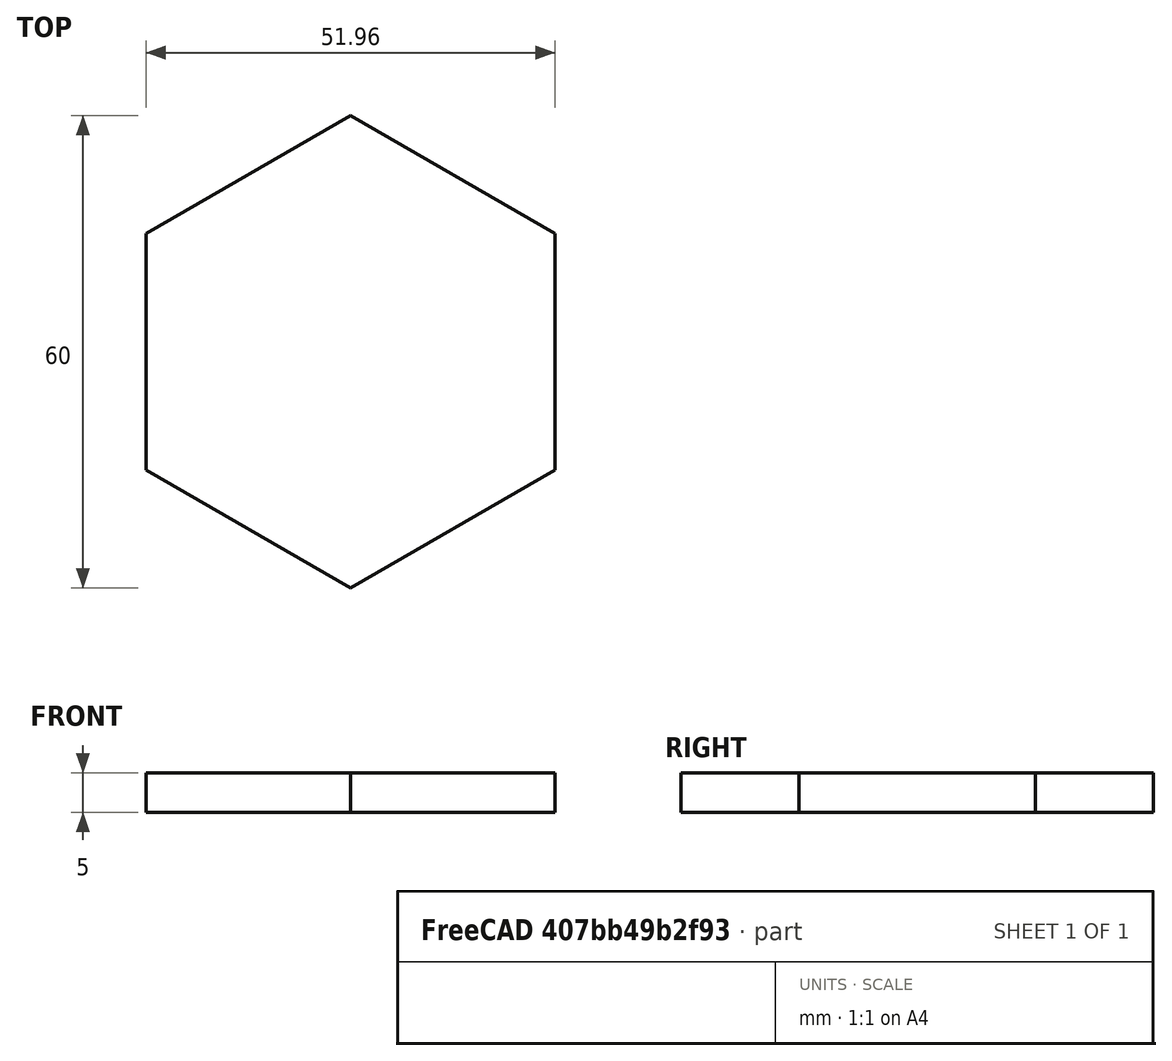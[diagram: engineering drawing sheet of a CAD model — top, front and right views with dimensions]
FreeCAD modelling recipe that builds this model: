
FCSTD DOCUMENT  (FreeCAD 0.19R)
Label: BodyTest
License: Creative Commons Attribution-ShareAlike
LicenseURL: http://creativecommons.org/licenses/by-sa/4.0/
objects: Sketcher::SketchObject×1, PartDesign::Pad×1, PartDesign::Body×1
note: 4 computed .brp shape members not serialized (recipe doc carries the construction recipe); baked Part::Feature solids carry a one-line shape summary decoded from their .brp

FEATURE [Sketcher::SketchObject] Sketch
  MapMode = 5
  Support = -> [XY_Plane001]
  sketch-geometry (7):
    g0: LineSegment StartX=25.9808 StartY=15 StartZ=0 EndX=3.6e-15 EndY=30 EndZ=0
    g1: LineSegment StartX=2e-15 StartY=30 StartZ=0 EndX=-25.9808 EndY=15 EndZ=0
    g2: LineSegment StartX=-25.9808 StartY=15 StartZ=0 EndX=-25.9808 EndY=-15 EndZ=0
    g3: LineSegment StartX=-25.9808 StartY=-15 StartZ=0 EndX=0 EndY=-30 EndZ=0
    g4: LineSegment StartX=0 StartY=-30 StartZ=0 EndX=25.9808 EndY=-15 EndZ=0
    g5: LineSegment StartX=25.9808 StartY=-15 StartZ=0 EndX=25.9808 EndY=15 EndZ=0
    g6: Circle [constr] CenterX=0 CenterY=0 CenterZ=0 NormalX=0 NormalY=0 NormalZ=1 AngleXU=0 Radius=30
  constraints (16):
    c: Coincident(g0,g1)
    c: Coincident(g1,g2)
    c: Coincident(g2,g3)
    c: Coincident(g3,g4)
    c: Coincident(g4,g5)
    c: Coincident(g5,g0)
    c: Equal(g0, g1-g5) x5
    c: PointOnObject(g0,g6)
    c: PointOnObject(g1,g6)
    c: PointOnObject(g2,g6)
    c: PointOnObject(g3,g6)
    c: PointOnObject(g4,g6)
    c: PointOnObject(g5,g6)
    c: Coincident(g6,g-1)
    c: Vertical(g5)
    c: Radius(g6) = 30
FEATURE [PartDesign::Pad] Pad
  Length = 5
  Length2 = 100
  Profile = -> Sketch
  Type = 0
FEATURE [PartDesign::Body] Body  label="Body_Hex"
  Group = -> [Sketch,Pad]
  Origin = -> Origin001
  Tip = -> Pad
